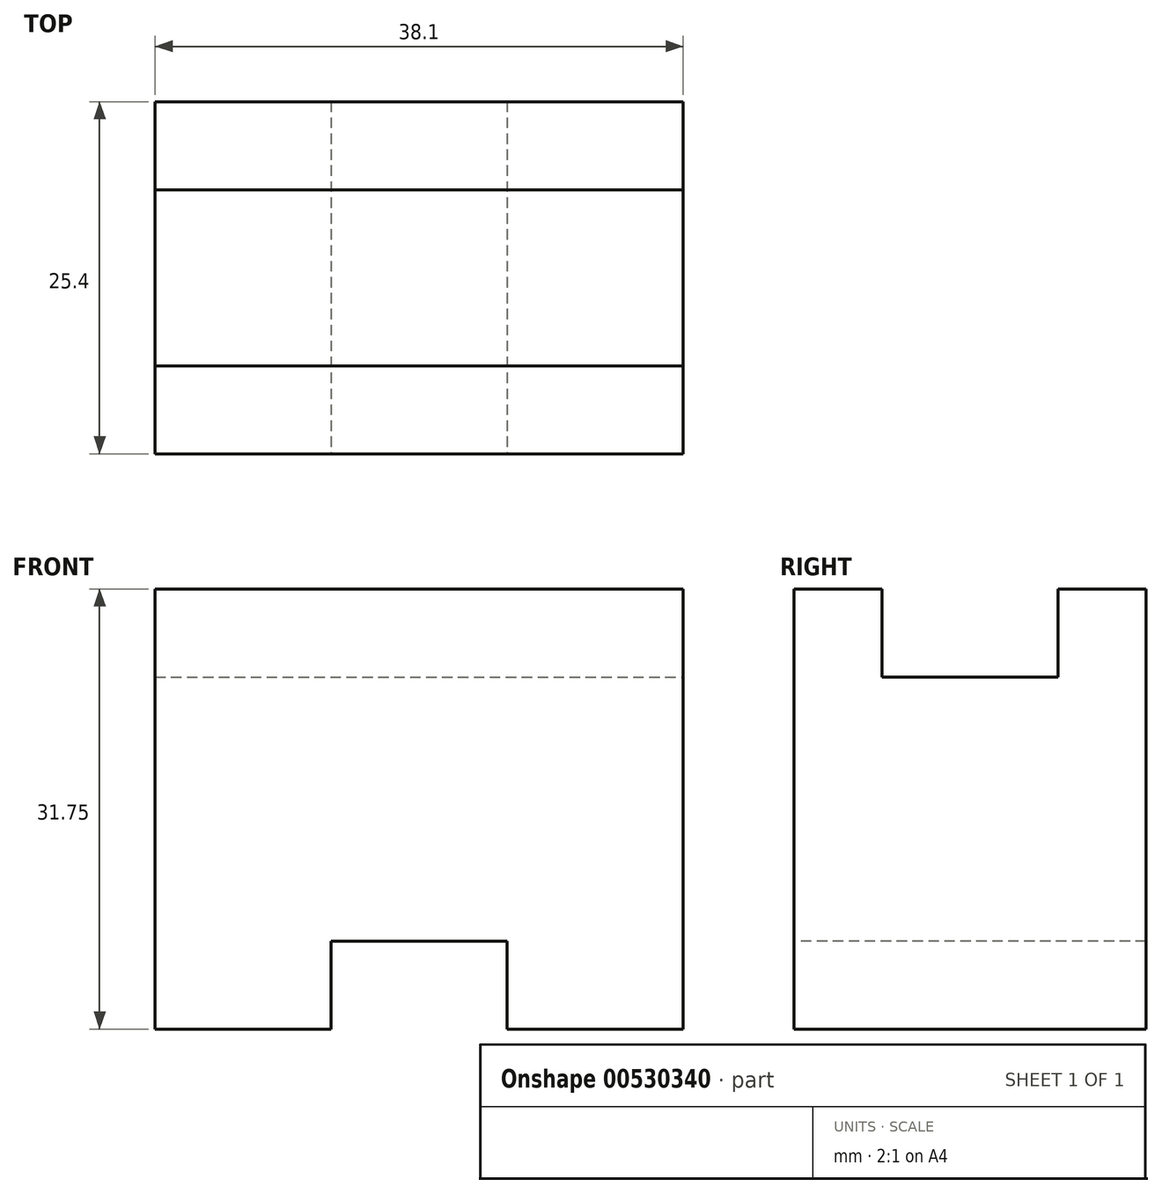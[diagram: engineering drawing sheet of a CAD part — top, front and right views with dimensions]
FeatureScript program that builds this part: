
annotation { "Feature Type Name" : "Feature", "Feature Type Description" : "" }
export const myFeature = defineFeature(function(context is Context, id is Id, definition is map)
    precondition{}
    {
        {
            var Q0;
            Q0=qCreatedBy(makeId("Right.planeOp"),FACE);
            var sketch = newSketch(context, id + "F0", { "sketchPlane" : qUnion([Q0])});
            skLineSegment(sketch, "E0", {"start": v(-14.75, 31.75) * mm, "end": v(-14.75, 0) * mm});
            skLineSegment(sketch, "E1", {"start": v(-14.75, 0) * mm, "end": v(10.65, 0) * mm});
            skLineSegment(sketch, "E2", {"start": v(10.65, 0) * mm, "end": v(10.65, 31.75) * mm});
            skLineSegment(sketch, "E3", {"start": v(10.65, 31.75) * mm, "end": v(-14.75, 31.75) * mm});
            skSolve(sketch);
        }
        {
            var Q0;
            Q0 = qSketchRegion(id + "F0", true);
            extrude(context, id + "F1", {"entities" : qUnion([Q0]), "depth" : 38.1 * mm, "offsetDistance" : 25.4 * mm});
        }
        {
            var Q0;
            Q0=makeQuery(id+"F1.opExtrude","CAP_FACE",FACE,{"disambiguationData":[OSD([sQuery(id+"F0.wireOp",EDGE,"E0"),sQuery(id+"F0.wireOp",EDGE,"E1"),sQuery(id+"F0.wireOp",EDGE,"E2"),sQuery(id+"F0.wireOp",EDGE,"E3")])],"isStart":false});
            var sketch = newSketch(context, id + "F2", { "sketchPlane" : qUnion([Q0])});
            skLineSegment(sketch, "E4", {"start": v(-8.4, 31.75) * mm, "end": v(-8.4, 25.4) * mm});
            skLineSegment(sketch, "E5", {"start": v(-8.4, 25.4) * mm, "end": v(4.3, 25.4) * mm});
            skLineSegment(sketch, "E6", {"start": v(4.3, 25.4) * mm, "end": v(4.3, 31.75) * mm});
            skLineSegment(sketch, "E7", {"start": v(4.3, 31.75) * mm, "end": v(-8.4, 31.75) * mm});
            skSolve(sketch);
        }
        {
            var Q0;
            Q0=makeQuery(id+"F2.imprint","IMPRINT",FACE,{"disambiguationData":[TD([[makeQuery(id+"F2.imprint","IMPRINT",EDGE,{"derivedFrom":sQuery(id+"F2.wireOp",EDGE,"E4")}),1.0]])]});
            extrude(context, id + "F3", {"entities" : qUnion([Q0]), "operationType" : NewBodyOperationType.REMOVE, "endBound" : BoundingType.THROUGH_ALL, "oppositeDirection" : true, "depth" : 25.4 * mm, "offsetDistance" : 25.4 * mm});
        }
        {
            var Q0;
            Q0=makeQuery(id+"F1.opExtrude","SWEPT_FACE",FACE,{"disambiguationData":[OSD([sQuery(id+"F0.wireOp",EDGE,"E0")])]});
            var sketch = newSketch(context, id + "F4", { "sketchPlane" : qUnion([Q0])});
            skLineSegment(sketch, "E8", {"start": v(12.7, 0) * mm, "end": v(12.7, 6.35) * mm});
            skLineSegment(sketch, "E9", {"start": v(12.7, 6.35) * mm, "end": v(25.4, 6.35) * mm});
            skLineSegment(sketch, "E10", {"start": v(25.4, 6.35) * mm, "end": v(25.4, 0) * mm});
            skLineSegment(sketch, "E11", {"start": v(25.4, 0) * mm, "end": v(12.7, 0) * mm});
            skSolve(sketch);
        }
        {
            var Q0;
            Q0=makeQuery(id+"F4.imprint","IMPRINT",FACE,{"disambiguationData":[TD([[makeQuery(id+"F4.imprint","IMPRINT",EDGE,{"derivedFrom":sQuery(id+"F4.wireOp",EDGE,"E8")}),-1.0]])]});
            extrude(context, id + "F5", {"entities" : qUnion([Q0]), "operationType" : NewBodyOperationType.REMOVE, "endBound" : BoundingType.THROUGH_ALL, "oppositeDirection" : true, "depth" : 25.4 * mm, "offsetDistance" : 25.4 * mm});
        }
    });
